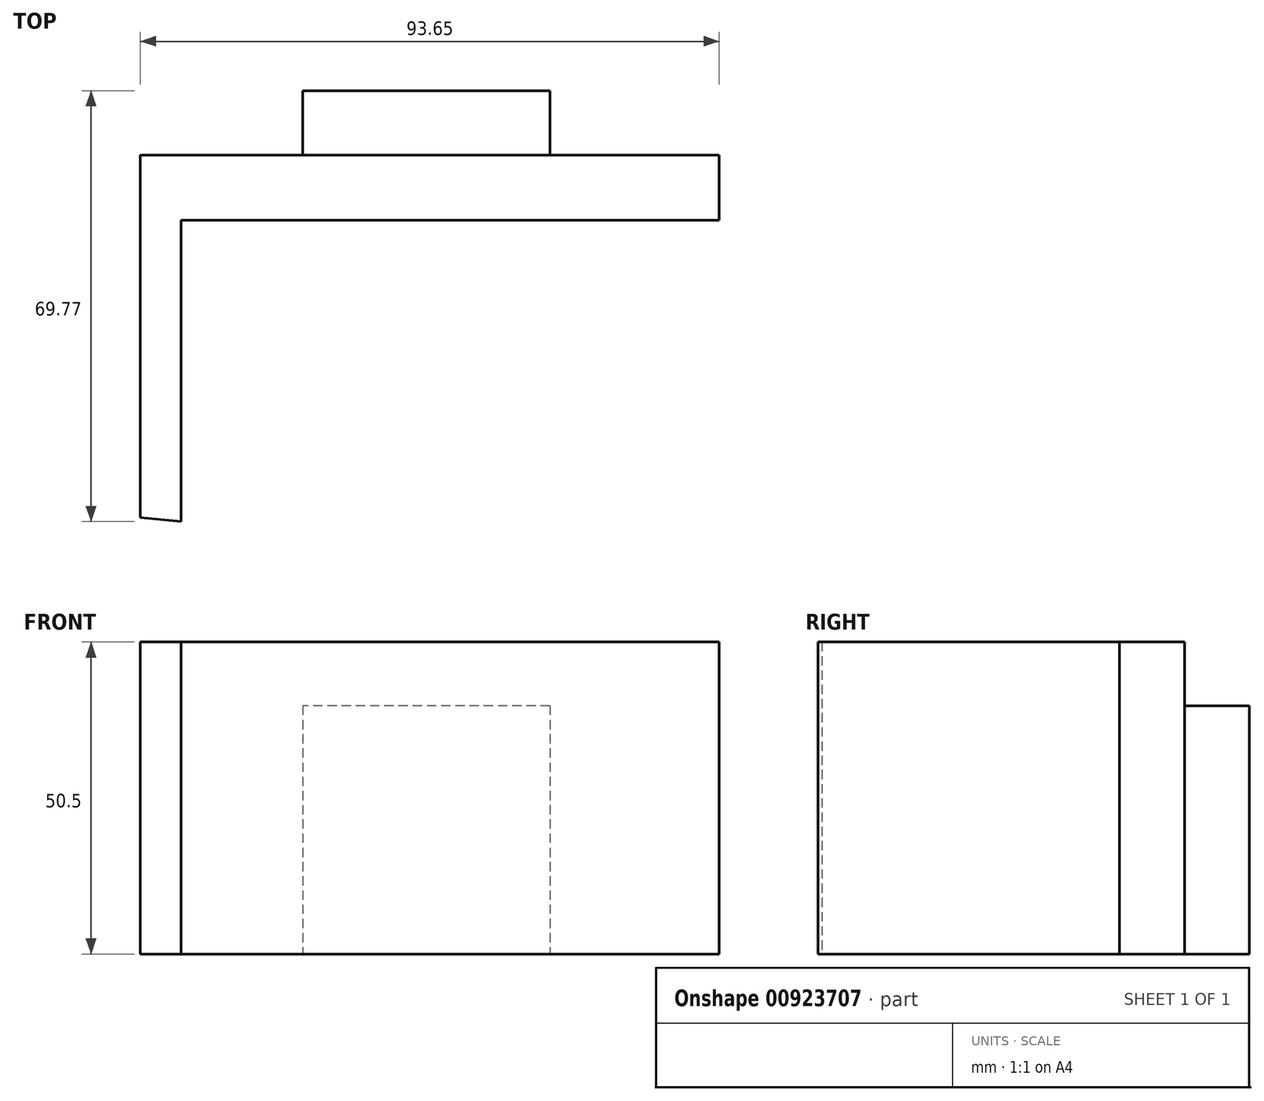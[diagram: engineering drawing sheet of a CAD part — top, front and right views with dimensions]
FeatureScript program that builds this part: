
annotation { "Feature Type Name" : "Feature", "Feature Type Description" : "" }
export const myFeature = defineFeature(function(context is Context, id is Id, definition is map)
    precondition{}
    {
        {
            var Q0;
            Q0=qCreatedBy(makeId("Top.planeOp"),FACE);
            var sketch = newSketch(context, id + "F0", { "sketchPlane" : qUnion([Q0])});
            skLineSegment(sketch, "E0", {"start": v(-55.27, -16.72) * mm, "end": v(-55.27, 41.93) * mm});
            skLineSegment(sketch, "E1", {"start": v(-55.27, 41.93) * mm, "end": v(38.38, 41.93) * mm});
            skLineSegment(sketch, "E2", {"start": v(38.38, 41.93) * mm, "end": v(38.38, 31.4) * mm});
            skLineSegment(sketch, "E3", {"start": v(38.38, 31.4) * mm, "end": v(-48.73, 31.4) * mm});
            skLineSegment(sketch, "E4", {"start": v(-48.73, 31.4) * mm, "end": v(-48.73, -17.37) * mm});
            skLineSegment(sketch, "E5", {"start": v(-48.73, -17.37) * mm, "end": v(-55.27, -16.72) * mm});
            skSolve(sketch);
        }
        {
            var Q0;
            Q0=makeQuery(id+"F0.imprint","IMPRINT",FACE,{"disambiguationData":[TD([[makeQuery(id+"F0.imprint","IMPRINT",EDGE,{"derivedFrom":sQuery(id+"F0.wireOp",EDGE,"E0")}),-1.0]])]});
            extrude(context, id + "F1", {"entities" : qUnion([Q0]), "depth" : 50.5 * mm, "offsetDistance" : 25 * mm});
        }
        {
            var Q0;
            Q0=makeQuery(id+"F1.opExtrude","SWEPT_FACE",FACE,{"disambiguationData":[OSD([sQuery(id+"F0.wireOp",EDGE,"E3")])]});
            var sketch = newSketch(context, id + "F2", { "sketchPlane" : qUnion([Q0])});
            skLineSegment(sketch, "E6.bottom", {"start": v(-29, 0) * mm, "end": v(11, 0) * mm});
            skLineSegment(sketch, "E6.top", {"start": v(-29, 40.2) * mm, "end": v(11, 40.2) * mm});
            skLineSegment(sketch, "E6.left", {"start": v(-29, 0) * mm, "end": v(-29, 40.2) * mm});
            skLineSegment(sketch, "E6.right", {"start": v(11, 0) * mm, "end": v(11, 40.2) * mm});
            skSolve(sketch);
        }
        {
            var Q0;
            Q0 = qSketchRegion(id + "F2", true);
            extrude(context, id + "F3", {"entities" : qUnion([Q0]), "operationType" : NewBodyOperationType.ADD, "oppositeDirection" : true, "depth" : 21 * mm, "offsetDistance" : 25 * mm});
        }
    });
